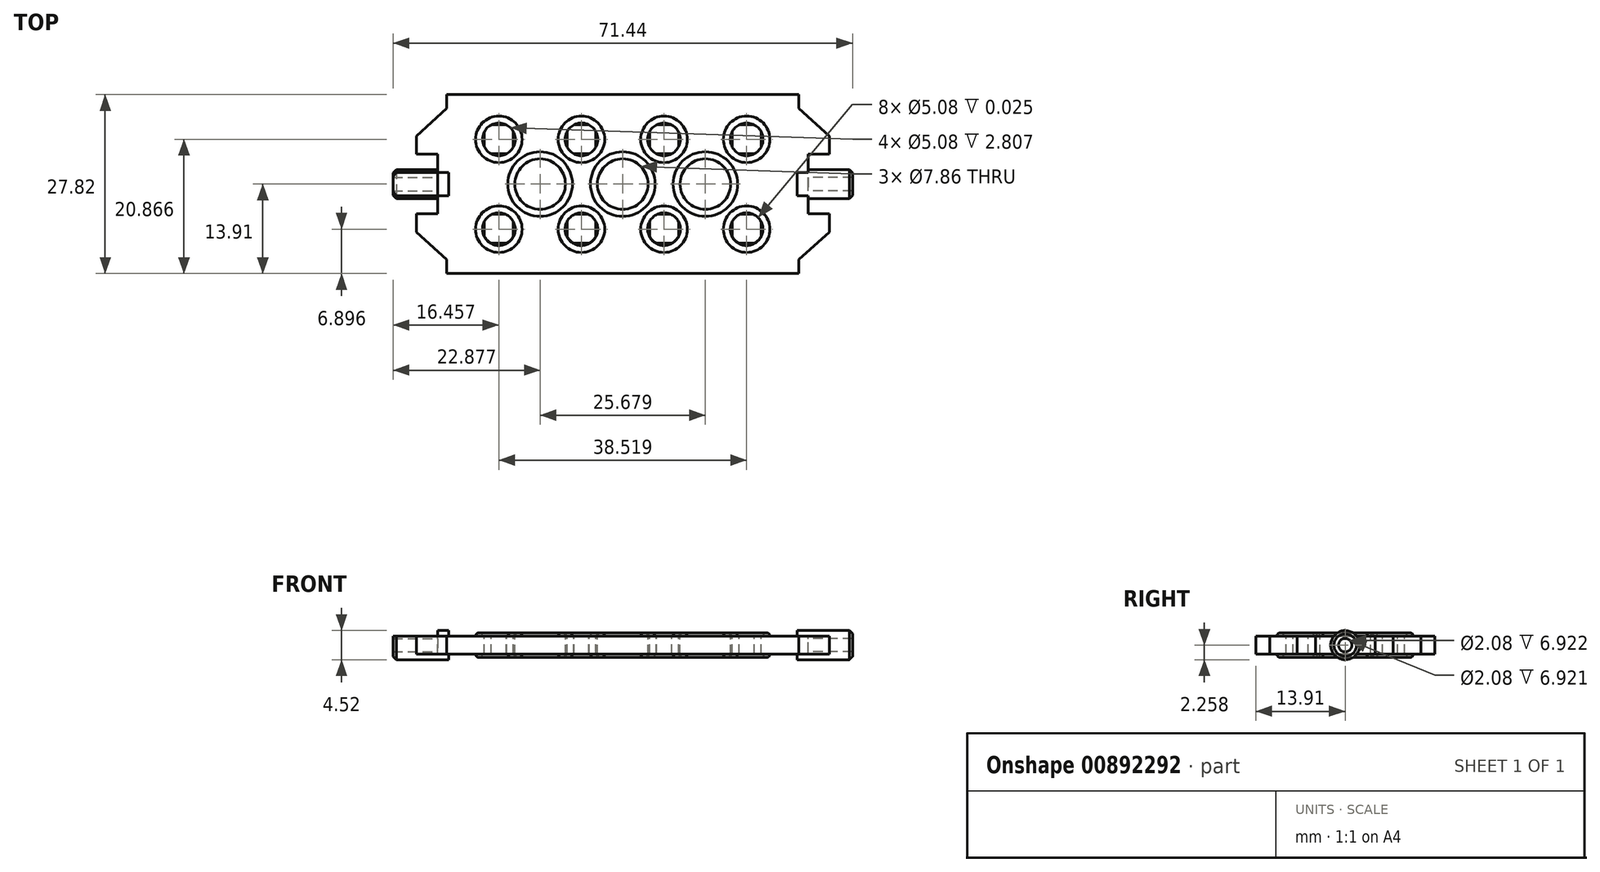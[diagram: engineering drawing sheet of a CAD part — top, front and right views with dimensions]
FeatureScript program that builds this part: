
annotation { "Feature Type Name" : "Feature", "Feature Type Description" : "" }
export const myFeature = defineFeature(function(context is Context, id is Id, definition is map)
    precondition{}
    {
        {
            var Q0;
            Q0=qCreatedBy(makeId("Top.planeOp"),FACE);
            var sketch = newSketch(context, id + "F0", { "sketchPlane" : qUnion([Q0])});
            skLineSegment(sketch, "E0.bottom", {"start": v(-32.7, 12.97) * mm, "end": v(31.5, 12.97) * mm});
            skLineSegment(sketch, "E0.top", {"start": v(-32.7, -14.85) * mm, "end": v(31.5, -14.85) * mm});
            skLineSegment(sketch, "E0.left", {"start": v(-32.7, 12.97) * mm, "end": v(-32.7, -14.85) * mm});
            skLineSegment(sketch, "E0.right", {"start": v(31.5, 12.97) * mm, "end": v(31.5, -14.85) * mm});
            skSolve(sketch);
        }
        {
            var Q0;
            Q0 = qSketchRegion(id + "F0", true);
            extrude(context, id + "F1", {"entities" : qUnion([Q0]), "depth" : 2.76 * mm, "offsetDistance" : 25.4 * mm});
        }
        {
            var Q0;
            Q0=makeQuery(id+"F1.opExtrude","CAP_FACE",FACE,{"disambiguationData":[OSD([sQuery(id+"F0.wireOp",EDGE,"E0.bottom"),sQuery(id+"F0.wireOp",EDGE,"E0.top"),sQuery(id+"F0.wireOp",EDGE,"E0.left"),sQuery(id+"F0.wireOp",EDGE,"E0.right")])],"isStart":false});
            var sketch = newSketch(context, id + "F2", { "sketchPlane" : qUnion([Q0])});
            skLineSegment(sketch, "E1", {"start": v(-32.7, -0.94) * mm, "end": v(31.5, -0.94) * mm, "construction": true});
            skPoint(sketch, "E2", {"position": v(26.78, 12.97) * mm});
            skLineSegment(sketch, "E3", {"start": v(28.2, 3.7) * mm, "end": v(28.2, -5.58) * mm});
            skLineSegment(sketch, "E4", {"start": v(26.78, 12.97) * mm, "end": v(26.78, 10.8) * mm});
            skLineSegment(sketch, "E5", {"start": v(28.2, 3.7) * mm, "end": v(31.5, 3.7) * mm});
            skLineSegment(sketch, "E6", {"start": v(28.2, -5.58) * mm, "end": v(31.5, -5.58) * mm});
            skLineSegment(sketch, "E7", {"start": v(28.2, -0.94) * mm, "end": v(28.2, -5.58) * mm});
            skLineSegment(sketch, "E8", {"start": v(31.5, -0.94) * mm, "end": v(31.5, 3.7) * mm});
            skLineSegment(sketch, "E9", {"start": v(31.5, 3.7) * mm, "end": v(31.5, 6.51) * mm});
            skLineSegment(sketch, "E10", {"start": v(31.5, -5.58) * mm, "end": v(31.5, -8.4) * mm});
            skPoint(sketch, "E11", {"position": v(26.78, -14.85) * mm});
            skLineSegment(sketch, "E12", {"start": v(26.78, -14.85) * mm, "end": v(26.78, -12.68) * mm});
            skLineSegment(sketch, "E13", {"start": v(26.78, -12.68) * mm, "end": v(31.5, -8.4) * mm});
            skLineSegment(sketch, "E14", {"start": v(26.78, 10.8) * mm, "end": v(31.5, 6.51) * mm});
            skPoint(sketch, "E15", {"position": v(-27.97, -14.85) * mm});
            skPoint(sketch, "E16", {"position": v(-27.97, 12.97) * mm});
            skLineSegment(sketch, "E17", {"start": v(-29.4, -0.94) * mm, "end": v(-29.4, 3.7) * mm});
            skLineSegment(sketch, "E18", {"start": v(-29.4, -0.94) * mm, "end": v(-29.4, -5.58) * mm});
            skLineSegment(sketch, "E19", {"start": v(-29.4, -5.58) * mm, "end": v(-32.7, -5.58) * mm});
            skLineSegment(sketch, "E20", {"start": v(-29.4, 3.7) * mm, "end": v(-32.7, 3.7) * mm});
            skLineSegment(sketch, "E21", {"start": v(-27.97, 12.97) * mm, "end": v(-27.97, 10.8) * mm});
            skLineSegment(sketch, "E22", {"start": v(-27.97, -14.85) * mm, "end": v(-27.97, -12.68) * mm});
            skLineSegment(sketch, "E23", {"start": v(-32.7, -5.58) * mm, "end": v(-32.7, -8.4) * mm});
            skLineSegment(sketch, "E24", {"start": v(-32.7, 3.7) * mm, "end": v(-32.7, 6.51) * mm});
            skLineSegment(sketch, "E25", {"start": v(-32.7, 6.51) * mm, "end": v(-27.97, 10.8) * mm});
            skLineSegment(sketch, "E26", {"start": v(-27.97, -12.68) * mm, "end": v(-32.7, -8.4) * mm});
            skCircle(sketch, "E27", {"center": v(-0.6, -0.94) * mm, "radius": 3.93 * mm});
            skLineSegment(sketch, "E28", {"start": v(31.5, 6.02) * mm, "end": v(-32.7, 6.02) * mm, "construction": true});
            skLineSegment(sketch, "E29", {"start": v(31.5, -0.94) * mm, "end": v(31.5, 12.97) * mm, "construction": true});
            skPoint(sketch, "E30", {"position": v(-7.01, 6.02) * mm});
            skPoint(sketch, "E31", {"position": v(5.83, 6.02) * mm});
            skPoint(sketch, "E32", {"position": v(18.67, 6.02) * mm});
            skPoint(sketch, "E33", {"position": v(31.5, 6.02) * mm});
            skPoint(sketch, "E34", {"position": v(-19.85, 6.02) * mm});
            skLineSegment(sketch, "E35", {"start": v(-19.85, -14.85) * mm, "end": v(-19.85, 6.02) * mm, "construction": true});
            skLineSegment(sketch, "E36", {"start": v(-7.01, 6.02) * mm, "end": v(-7.01, -14.85) * mm, "construction": true});
            skLineSegment(sketch, "E37", {"start": v(5.83, 6.02) * mm, "end": v(5.83, -14.85) * mm, "construction": true});
            skLineSegment(sketch, "E38", {"start": v(18.67, 6.02) * mm, "end": v(18.67, -14.85) * mm, "construction": true});
            skLineSegment(sketch, "E39", {"start": v(31.5, -0.94) * mm, "end": v(31.5, -14.85) * mm, "construction": true});
            skPoint(sketch, "E40", {"position": v(31.5, -7.9) * mm});
            skLineSegment(sketch, "E41", {"start": v(31.5, -7.9) * mm, "end": v(-32.7, -7.9) * mm, "construction": true});
            skCircle(sketch, "E42", {"center": v(-19.85, -7.9) * mm, "radius": 2.54 * mm});
            skCircle(sketch, "E43", {"center": v(-19.85, 6.02) * mm, "radius": 2.54 * mm});
            skCircle(sketch, "E44", {"center": v(-7.01, 6.02) * mm, "radius": 2.54 * mm});
            skCircle(sketch, "E45", {"center": v(5.83, 6.02) * mm, "radius": 2.54 * mm});
            skCircle(sketch, "E46", {"center": v(18.67, 6.02) * mm, "radius": 2.54 * mm});
            skCircle(sketch, "E47", {"center": v(-7.01, -7.9) * mm, "radius": 2.54 * mm});
            skCircle(sketch, "E48", {"center": v(18.67, -7.9) * mm, "radius": 2.54 * mm});
            skCircle(sketch, "E49", {"center": v(5.83, -7.9) * mm, "radius": 2.54 * mm});
            skPoint(sketch, "E50", {"position": v(5.83, -0.94) * mm});
            skPoint(sketch, "E51", {"position": v(18.67, -0.94) * mm});
            skPoint(sketch, "E52", {"position": v(-7.01, -0.94) * mm});
            skPoint(sketch, "E53", {"position": v(-19.85, -0.94) * mm});
            skLineSegment(sketch, "E54", {"start": v(18.67, -0.94) * mm, "end": v(5.83, -0.94) * mm});
            skLineSegment(sketch, "E55", {"start": v(-19.85, -0.94) * mm, "end": v(-7.01, -0.94) * mm});
            skCircle(sketch, "E56", {"center": v(12.25, -0.94) * mm, "radius": 3.93 * mm});
            skCircle(sketch, "E57", {"center": v(-13.43, -0.94) * mm, "radius": 3.93 * mm});
            skLineSegment(sketch, "E58.bottom", {"start": v(16.42, -10.14) * mm, "end": v(20.91, -10.14) * mm});
            skLineSegment(sketch, "E58.top", {"start": v(16.42, -5.65) * mm, "end": v(20.91, -5.65) * mm});
            skLineSegment(sketch, "E58.left", {"start": v(16.42, -10.14) * mm, "end": v(16.42, -5.65) * mm});
            skLineSegment(sketch, "E58.right", {"start": v(20.91, -10.14) * mm, "end": v(20.91, -5.65) * mm});
            skLineSegment(sketch, "E59.0.1.0", {"start": v(16.42, 3.77) * mm, "end": v(20.91, 3.77) * mm});
            skLineSegment(sketch, "E59.0.1.1", {"start": v(16.42, 3.77) * mm, "end": v(16.42, 8.27) * mm});
            skLineSegment(sketch, "E59.0.1.2", {"start": v(16.42, 8.27) * mm, "end": v(20.91, 8.27) * mm});
            skLineSegment(sketch, "E59.0.1.3", {"start": v(20.91, 3.77) * mm, "end": v(20.91, 8.27) * mm});
            skLineSegment(sketch, "E59.1.0.0", {"start": v(3.58, -10.14) * mm, "end": v(8.07, -10.14) * mm});
            skLineSegment(sketch, "E59.1.0.1", {"start": v(3.58, -10.14) * mm, "end": v(3.58, -5.65) * mm});
            skLineSegment(sketch, "E59.1.0.2", {"start": v(3.58, -5.65) * mm, "end": v(8.07, -5.65) * mm});
            skLineSegment(sketch, "E59.1.0.3", {"start": v(8.07, -10.14) * mm, "end": v(8.07, -5.65) * mm});
            skLineSegment(sketch, "E59.1.1.0", {"start": v(3.58, 3.77) * mm, "end": v(8.07, 3.77) * mm});
            skLineSegment(sketch, "E59.1.1.1", {"start": v(3.58, 3.77) * mm, "end": v(3.58, 8.27) * mm});
            skLineSegment(sketch, "E59.1.1.2", {"start": v(3.58, 8.27) * mm, "end": v(8.07, 8.27) * mm});
            skLineSegment(sketch, "E59.1.1.3", {"start": v(8.07, 3.77) * mm, "end": v(8.07, 8.27) * mm});
            skLineSegment(sketch, "E59.2.0.0", {"start": v(-9.26, -10.14) * mm, "end": v(-4.76, -10.14) * mm});
            skLineSegment(sketch, "E59.2.0.1", {"start": v(-9.26, -10.14) * mm, "end": v(-9.26, -5.65) * mm});
            skLineSegment(sketch, "E59.2.0.2", {"start": v(-9.26, -5.65) * mm, "end": v(-4.76, -5.65) * mm});
            skLineSegment(sketch, "E59.2.0.3", {"start": v(-4.76, -10.14) * mm, "end": v(-4.76, -5.65) * mm});
            skLineSegment(sketch, "E59.2.1.0", {"start": v(-9.26, 3.77) * mm, "end": v(-4.76, 3.77) * mm});
            skLineSegment(sketch, "E59.2.1.1", {"start": v(-9.26, 3.77) * mm, "end": v(-9.26, 8.27) * mm});
            skLineSegment(sketch, "E59.2.1.2", {"start": v(-9.26, 8.27) * mm, "end": v(-4.76, 8.27) * mm});
            skLineSegment(sketch, "E59.2.1.3", {"start": v(-4.76, 3.77) * mm, "end": v(-4.76, 8.27) * mm});
            skLineSegment(sketch, "E59.3.0.0", {"start": v(-22.1, -10.14) * mm, "end": v(-17.6, -10.14) * mm});
            skLineSegment(sketch, "E59.3.0.1", {"start": v(-22.1, -10.14) * mm, "end": v(-22.1, -5.65) * mm});
            skLineSegment(sketch, "E59.3.0.2", {"start": v(-22.1, -5.65) * mm, "end": v(-17.6, -5.65) * mm});
            skLineSegment(sketch, "E59.3.0.3", {"start": v(-17.6, -10.14) * mm, "end": v(-17.6, -5.65) * mm});
            skLineSegment(sketch, "E59.3.1.0", {"start": v(-22.1, 3.77) * mm, "end": v(-17.6, 3.77) * mm});
            skLineSegment(sketch, "E59.3.1.1", {"start": v(-22.1, 3.77) * mm, "end": v(-22.1, 8.27) * mm});
            skLineSegment(sketch, "E59.3.1.2", {"start": v(-22.1, 8.27) * mm, "end": v(-17.6, 8.27) * mm});
            skLineSegment(sketch, "E59.3.1.3", {"start": v(-17.6, 3.77) * mm, "end": v(-17.6, 8.27) * mm});
            skLineSegment(sketch, "E59.direction1", {"start": v(16.42, -10.14) * mm, "end": v(3.58, -10.14) * mm, "construction": true});
            skLineSegment(sketch, "E59.direction2", {"start": v(16.42, -10.14) * mm, "end": v(16.42, 3.77) * mm, "construction": true});
            skSolve(sketch);
        }
        {
            var Q0;
            Q0=makeQuery(id+"F2.imprint","IMPRINT",FACE,{"disambiguationData":[TD([[makeQuery(id+"F2.imprint","IMPRINT",EDGE,{"derivedFrom":sQuery(id+"F2.wireOp",EDGE,"E3")}),1.0]])]});
            var Q1;
            {var subQ0=sQuery(id+"F2.wireOp",EDGE,"E4");Q1=makeQuery(id+"F2.imprint","IMPRINT",FACE,{"disambiguationData":[TD([[makeQuery(id+"F2.imprint","IMPRINT",EDGE,{"derivedFrom":subQ0}),1.0]])]});}
            var Q2;
            {var subQ0=sQuery(id+"F2.wireOp",EDGE,"E12");Q2=makeQuery(id+"F2.imprint","IMPRINT",FACE,{"disambiguationData":[TD([[makeQuery(id+"F2.imprint","IMPRINT",EDGE,{"derivedFrom":subQ0}),-1.0]])]});}
            var Q3;
            {var subQ0=sQuery(id+"F2.wireOp",EDGE,"E22");Q3=makeQuery(id+"F2.imprint","IMPRINT",FACE,{"disambiguationData":[TD([[makeQuery(id+"F2.imprint","IMPRINT",EDGE,{"derivedFrom":subQ0}),1.0]])]});}
            var Q4;
            Q4=makeQuery(id+"F2.imprint","IMPRINT",FACE,{"disambiguationData":[TD([[makeQuery(id+"F2.imprint","IMPRINT",EDGE,{"derivedFrom":sQuery(id+"F2.wireOp",EDGE,"E17")}),1.0]])]});
            var Q5;
            {var subQ0=sQuery(id+"F2.wireOp",EDGE,"E21");Q5=makeQuery(id+"F2.imprint","IMPRINT",FACE,{"disambiguationData":[TD([[makeQuery(id+"F2.imprint","IMPRINT",EDGE,{"derivedFrom":subQ0}),-1.0]])]});}
            extrude(context, id + "F3", {"entities" : qUnion([Q0, Q1, Q2, Q3, Q4, Q5]), "operationType" : NewBodyOperationType.REMOVE, "oppositeDirection" : true, "depth" : 25.4 * mm, "offsetDistance" : 25.4 * mm});
        }
        {
            var Q0;
            Q0=makeQuery(id+"F2.imprint","IMPRINT",FACE,{"disambiguationData":[TD([[makeQuery(id+"F2.imprint","IMPRINT",EDGE,{"derivedFrom":sQuery(id+"F2.wireOp",EDGE,"E43")}),1.0]])]});
            var Q1;
            {var subQ0=sQuery(id+"F2.wireOp",EDGE,"E57");var subQ1=sQuery(id+"F2.wireOp",EDGE,"E55");var subQ2=makeQuery(id+"F2.imprint","INTERSECT",VERTEX,{"disambiguationData":[OD(0.0)],"derivedFrom":[subQ1,subQ0]});Q1=makeQuery(id+"F2.imprint","IMPRINT",FACE,{"disambiguationData":[TD([[makeQuery(id+"F2.imprint","IMPRINT",EDGE,{"disambiguationData":[TD([[subQ2,-1.0]])],"derivedFrom":subQ1}),-1.0]])]});}
            var Q2;
            {var subQ0=sQuery(id+"F2.wireOp",EDGE,"E57");var subQ1=sQuery(id+"F2.wireOp",EDGE,"E55");var subQ2=makeQuery(id+"F2.imprint","INTERSECT",VERTEX,{"disambiguationData":[OD(0.0)],"derivedFrom":[subQ1,subQ0]});Q2=makeQuery(id+"F2.imprint","IMPRINT",FACE,{"disambiguationData":[TD([[makeQuery(id+"F2.imprint","IMPRINT",EDGE,{"disambiguationData":[TD([[subQ2,-1.0]])],"derivedFrom":subQ1}),1.0]])]});}
            var Q3;
            Q3=makeQuery(id+"F2.imprint","IMPRINT",FACE,{"disambiguationData":[TD([[makeQuery(id+"F2.imprint","IMPRINT",EDGE,{"derivedFrom":sQuery(id+"F2.wireOp",EDGE,"E27")}),1.0]])]});
            var Q4;
            {var subQ0=sQuery(id+"F2.wireOp",EDGE,"E56");var subQ1=sQuery(id+"F2.wireOp",EDGE,"E54");var subQ2=makeQuery(id+"F2.imprint","INTERSECT",VERTEX,{"disambiguationData":[OD(0.0)],"derivedFrom":[subQ1,subQ0]});Q4=makeQuery(id+"F2.imprint","IMPRINT",FACE,{"disambiguationData":[TD([[makeQuery(id+"F2.imprint","IMPRINT",EDGE,{"disambiguationData":[TD([[subQ2,1.0]])],"derivedFrom":subQ1}),1.0]])]});}
            var Q5;
            {var subQ0=sQuery(id+"F2.wireOp",EDGE,"E56");var subQ1=sQuery(id+"F2.wireOp",EDGE,"E54");var subQ2=makeQuery(id+"F2.imprint","INTERSECT",VERTEX,{"disambiguationData":[OD(0.0)],"derivedFrom":[subQ1,subQ0]});Q5=makeQuery(id+"F2.imprint","IMPRINT",FACE,{"disambiguationData":[TD([[makeQuery(id+"F2.imprint","IMPRINT",EDGE,{"disambiguationData":[TD([[subQ2,1.0]])],"derivedFrom":subQ1}),-1.0]])]});}
            var Q6;
            Q6=makeQuery(id+"F2.imprint","IMPRINT",FACE,{"disambiguationData":[TD([[makeQuery(id+"F2.imprint","IMPRINT",EDGE,{"derivedFrom":sQuery(id+"F2.wireOp",EDGE,"E45")}),1.0]])]});
            var Q7;
            Q7=makeQuery(id+"F2.imprint","IMPRINT",FACE,{"disambiguationData":[TD([[makeQuery(id+"F2.imprint","IMPRINT",EDGE,{"derivedFrom":sQuery(id+"F2.wireOp",EDGE,"E44")}),1.0]])]});
            var Q8;
            Q8=makeQuery(id+"F2.imprint","IMPRINT",FACE,{"disambiguationData":[TD([[makeQuery(id+"F2.imprint","IMPRINT",EDGE,{"derivedFrom":sQuery(id+"F2.wireOp",EDGE,"E47")}),1.0]])]});
            var Q9;
            Q9=makeQuery(id+"F2.imprint","IMPRINT",FACE,{"disambiguationData":[TD([[makeQuery(id+"F2.imprint","IMPRINT",EDGE,{"derivedFrom":sQuery(id+"F2.wireOp",EDGE,"E42")}),1.0]])]});
            var Q10;
            Q10=makeQuery(id+"F2.imprint","IMPRINT",FACE,{"disambiguationData":[TD([[makeQuery(id+"F2.imprint","IMPRINT",EDGE,{"derivedFrom":sQuery(id+"F2.wireOp",EDGE,"E49")}),1.0]])]});
            var Q11;
            Q11=makeQuery(id+"F2.imprint","IMPRINT",FACE,{"disambiguationData":[TD([[makeQuery(id+"F2.imprint","IMPRINT",EDGE,{"derivedFrom":sQuery(id+"F2.wireOp",EDGE,"E48")}),1.0]])]});
            var Q12;
            Q12=makeQuery(id+"F2.imprint","IMPRINT",FACE,{"disambiguationData":[TD([[makeQuery(id+"F2.imprint","IMPRINT",EDGE,{"derivedFrom":sQuery(id+"F2.wireOp",EDGE,"E46")}),1.0]])]});
            extrude(context, id + "F4", {"entities" : qUnion([Q0, Q1, Q2, Q3, Q4, Q5, Q6, Q7, Q8, Q9, Q10, Q11, Q12]), "operationType" : NewBodyOperationType.REMOVE, "oppositeDirection" : true, "depth" : 25.4 * mm, "offsetDistance" : 25.4 * mm});
        }
        {
            var Q0;
            Q0=makeQuery(id+"F3.boolean.opBoolean","COPY",FACE,{"derivedFrom":makeQuery(id+"F3.opExtrude","SWEPT_FACE",FACE,{"disambiguationData":[OSD([sQuery(id+"F2.wireOp",EDGE,"E17"),sQuery(id+"F2.wireOp",EDGE,"E18")])]})});
            var sketch = newSketch(context, id + "F5", { "sketchPlane" : qUnion([Q0])});
            skLineSegment(sketch, "E60", {"start": v(0.94, 0) * mm, "end": v(0.94, 2.76) * mm, "construction": true});
            skCircle(sketch, "E61", {"center": v(0.94, 1.38) * mm, "radius": 2.26 * mm});
            skCircle(sketch, "E62", {"center": v(0.94, 1.38) * mm, "radius": 1.04 * mm});
            skSolve(sketch);
        }
        {
            var Q0;
            Q0=makeQuery(id+"F5.imprint","IMPRINT",FACE,{"disambiguationData":[TD([[makeQuery(id+"F5.imprint","IMPRINT",EDGE,{"derivedFrom":sQuery(id+"F5.wireOp",EDGE,"E62")}),-1.0]])]});
            var Q1;
            {var subQ0=sQuery(id+"F5.wireOp",EDGE,"E61");var subQ1=makeQuery(id+"F3.boolean.opBoolean","COPY",EDGE,{"derivedFrom":makeQuery(id+"F3.opExtrude","CAP_EDGE",EDGE,{"disambiguationData":[OSD([sQuery(id+"F2.wireOp",EDGE,"E17"),sQuery(id+"F2.wireOp",EDGE,"E18")])],"isStart":true})});var subQ2=makeQuery(id+"F5.imprint","INTERSECT",VERTEX,{"disambiguationData":[OD(0.0)],"derivedFrom":[subQ1,subQ0]});Q1=makeQuery(id+"F5.imprint","IMPRINT",FACE,{"disambiguationData":[TD([[makeQuery(id+"F5.imprint","IMPRINT",EDGE,{"disambiguationData":[TD([[subQ2,1.0]])],"derivedFrom":subQ0}),1.0]])]});}
            var Q2;
            {var subQ0=sQuery(id+"F5.wireOp",EDGE,"E61");var subQ1=makeQuery(id+"F3.boolean.opBoolean","INTERSECT",EDGE,{"derivedFrom":[makeQuery(id+"F1.opExtrude","CAP_FACE",FACE,{"disambiguationData":[OSD([sQuery(id+"F0.wireOp",EDGE,"E0.bottom"),sQuery(id+"F0.wireOp",EDGE,"E0.top"),sQuery(id+"F0.wireOp",EDGE,"E0.left"),sQuery(id+"F0.wireOp",EDGE,"E0.right")])],"isStart":true}),makeQuery(id+"F3.opExtrude","SWEPT_FACE",FACE,{"disambiguationData":[OSD([sQuery(id+"F2.wireOp",EDGE,"E17"),sQuery(id+"F2.wireOp",EDGE,"E18")])]})]});var subQ2=makeQuery(id+"F5.imprint","INTERSECT",VERTEX,{"disambiguationData":[OD(0.0)],"derivedFrom":[subQ1,subQ0]});Q2=makeQuery(id+"F5.imprint","IMPRINT",FACE,{"disambiguationData":[TD([[makeQuery(id+"F5.imprint","IMPRINT",EDGE,{"disambiguationData":[TD([[subQ2,-1.0]])],"derivedFrom":subQ0}),1.0]])]});}
            extrude(context, id + "F6", {"entities" : qUnion([Q0, Q1, Q2]), "operationType" : NewBodyOperationType.ADD, "depth" : 6.92 * mm, "offsetDistance" : 25.4 * mm});
        }
        {
            var Q0;
            Q0=makeQuery(id+"F3.boolean.opBoolean","COPY",FACE,{"derivedFrom":makeQuery(id+"F3.opExtrude","SWEPT_FACE",FACE,{"disambiguationData":[OSD([sQuery(id+"F2.wireOp",EDGE,"E3"),sQuery(id+"F2.wireOp",EDGE,"E7")])]})});
            var sketch = newSketch(context, id + "F7", { "sketchPlane" : qUnion([Q0])});
            skCircle(sketch, "E63.0", {"center": v(-0.94, 1.38) * mm, "radius": 2.26 * mm});
            skCircle(sketch, "E63.1", {"center": v(-0.94, 1.38) * mm, "radius": 1.04 * mm});
            skSolve(sketch);
        }
        {
            var Q0;
            Q0 = qSketchRegion(id + "F7", true);
            extrude(context, id + "F8", {"entities" : qUnion([Q0]), "operationType" : NewBodyOperationType.ADD, "depth" : 6.92 * mm, "offsetDistance" : 25.4 * mm});
        }
        {
            var Q0;
            {var subQ0=sQuery(id+"F5.wireOp",EDGE,"E61");Q0=makeQuery(id+"F6.boolean.opBoolean","SPLIT",FACE,{"disambiguationData":[TD([makeQuery(id+"F1.opExtrude","CAP_FACE",FACE,{"disambiguationData":[OSD([sQuery(id+"F0.wireOp",EDGE,"E0.bottom"),sQuery(id+"F0.wireOp",EDGE,"E0.top"),sQuery(id+"F0.wireOp",EDGE,"E0.left"),sQuery(id+"F0.wireOp",EDGE,"E0.right")])],"isStart":false})])],"derivedFrom":makeQuery(id+"F6.opExtrude","CAP_FACE",FACE,{"disambiguationData":[OSD([subQ0,sQuery(id+"F5.wireOp",EDGE,"E62")])],"isStart":true})});}
            var sketch = newSketch(context, id + "F9", { "sketchPlane" : qUnion([Q0])});
            skCircle(sketch, "E64.0.0", {"center": v(-0.94, 1.38) * mm, "radius": 2.26 * mm});
            skSolve(sketch);
        }
        {
            var Q0;
            Q0 = qSketchRegion(id + "F9", true);
            extrude(context, id + "F10", {"entities" : qUnion([Q0]), "operationType" : NewBodyOperationType.ADD, "depth" : 1.71 * mm, "offsetDistance" : 25.4 * mm});
        }
        {
            var Q0;
            {var subQ0=sQuery(id+"F7.wireOp",EDGE,"E63.0");Q0=makeQuery(id+"F8.boolean.opBoolean","SPLIT",FACE,{"disambiguationData":[TD([makeQuery(id+"F1.opExtrude","CAP_FACE",FACE,{"disambiguationData":[OSD([sQuery(id+"F0.wireOp",EDGE,"E0.bottom"),sQuery(id+"F0.wireOp",EDGE,"E0.top"),sQuery(id+"F0.wireOp",EDGE,"E0.left"),sQuery(id+"F0.wireOp",EDGE,"E0.right")])],"isStart":false})])],"derivedFrom":makeQuery(id+"F8.opExtrude","CAP_FACE",FACE,{"disambiguationData":[OSD([subQ0,sQuery(id+"F7.wireOp",EDGE,"E63.1")])],"isStart":true})});}
            var sketch = newSketch(context, id + "F11", { "sketchPlane" : qUnion([Q0])});
            skCircle(sketch, "E65.0", {"center": v(0.94, 1.38) * mm, "radius": 2.26 * mm});
            skCircle(sketch, "E65.1", {"center": v(0.94, 1.38) * mm, "radius": 1.04 * mm});
            skSolve(sketch);
        }
        {
            var Q0;
            Q0 = qSketchRegion(id + "F11", true);
            extrude(context, id + "F12", {"entities" : qUnion([Q0]), "operationType" : NewBodyOperationType.ADD, "depth" : 1.71 * mm, "offsetDistance" : 25.4 * mm});
        }
        {
            var Q0;
            Q0=makeQuery(id+"F1.opExtrude","CAP_FACE",FACE,{"disambiguationData":[OSD([sQuery(id+"F0.wireOp",EDGE,"E0.bottom"),sQuery(id+"F0.wireOp",EDGE,"E0.top"),sQuery(id+"F0.wireOp",EDGE,"E0.left"),sQuery(id+"F0.wireOp",EDGE,"E0.right")])],"isStart":false});
            var sketch = newSketch(context, id + "F13", { "sketchPlane" : qUnion([Q0])});
            skCircle(sketch, "E66", {"center": v(-19.85, 6.02) * mm, "radius": 3.62 * mm});
            skCircle(sketch, "E67.0", {"center": v(-19.85, 6.02) * mm, "radius": 2.54 * mm});
            skCircle(sketch, "E68.0.1.0", {"center": v(-19.85, -7.95) * mm, "radius": 2.54 * mm});
            skCircle(sketch, "E68.0.1.1", {"center": v(-19.85, -7.95) * mm, "radius": 3.62 * mm});
            skCircle(sketch, "E68.1.0.0", {"center": v(-7.01, 6.02) * mm, "radius": 2.54 * mm});
            skCircle(sketch, "E68.1.0.1", {"center": v(-7.01, 6.02) * mm, "radius": 3.62 * mm});
            skCircle(sketch, "E68.1.1.0", {"center": v(-7.01, -7.95) * mm, "radius": 2.54 * mm});
            skCircle(sketch, "E68.1.1.1", {"center": v(-7.01, -7.95) * mm, "radius": 3.62 * mm});
            skCircle(sketch, "E68.2.0.0", {"center": v(5.83, 6.02) * mm, "radius": 2.54 * mm});
            skCircle(sketch, "E68.2.0.1", {"center": v(5.83, 6.02) * mm, "radius": 3.62 * mm});
            skCircle(sketch, "E68.2.1.0", {"center": v(5.83, -7.95) * mm, "radius": 2.54 * mm});
            skCircle(sketch, "E68.2.1.1", {"center": v(5.83, -7.95) * mm, "radius": 3.62 * mm});
            skCircle(sketch, "E68.3.0.0", {"center": v(18.67, 6.02) * mm, "radius": 2.54 * mm});
            skCircle(sketch, "E68.3.0.1", {"center": v(18.67, 6.02) * mm, "radius": 3.62 * mm});
            skCircle(sketch, "E68.3.1.0", {"center": v(18.67, -7.95) * mm, "radius": 2.54 * mm});
            skCircle(sketch, "E68.3.1.1", {"center": v(18.67, -7.95) * mm, "radius": 3.62 * mm});
            skLineSegment(sketch, "E68.direction1", {"start": v(-19.85, 6.02) * mm, "end": v(-7.01, 6.02) * mm, "construction": true});
            skLineSegment(sketch, "E68.direction2", {"start": v(-19.85, 6.02) * mm, "end": v(-19.85, -7.95) * mm, "construction": true});
            skCircle(sketch, "E69", {"center": v(12.25, -0.94) * mm, "radius": 5.02 * mm});
            skCircle(sketch, "E70", {"center": v(-0.6, -0.94) * mm, "radius": 5.02 * mm});
            skCircle(sketch, "E71", {"center": v(-13.43, -0.94) * mm, "radius": 5.02 * mm});
            skCircle(sketch, "E72.0", {"center": v(12.25, -0.94) * mm, "radius": 3.93 * mm});
            skCircle(sketch, "E72.1", {"center": v(-0.6, -0.94) * mm, "radius": 3.93 * mm});
            skCircle(sketch, "E72.2", {"center": v(-13.43, -0.94) * mm, "radius": 3.93 * mm});
            skSolve(sketch);
        }
        {
            var Q0;
            Q0 = qSketchRegion(id + "F13", true);
            extrude(context, id + "F14", {"entities" : qUnion([Q0]), "operationType" : NewBodyOperationType.ADD, "depth" : 0.53 * mm, "offsetDistance" : 25.4 * mm});
        }
        {
            var Q0;
            Q0=makeQuery(id+"F1.opExtrude","CAP_FACE",FACE,{"disambiguationData":[OSD([sQuery(id+"F0.wireOp",EDGE,"E0.bottom"),sQuery(id+"F0.wireOp",EDGE,"E0.top"),sQuery(id+"F0.wireOp",EDGE,"E0.left"),sQuery(id+"F0.wireOp",EDGE,"E0.right")])],"isStart":true});
            var sketch = newSketch(context, id + "F15", { "sketchPlane" : qUnion([Q0])});
            skCircle(sketch, "E73.0", {"center": v(-19.85, -6.02) * mm, "radius": 2.54 * mm});
            skCircle(sketch, "E73.1", {"center": v(-19.85, -6.02) * mm, "radius": 3.62 * mm});
            skCircle(sketch, "E74.0.1.0", {"center": v(-19.85, 7.95) * mm, "radius": 3.62 * mm});
            skCircle(sketch, "E74.0.1.1", {"center": v(-19.85, 7.95) * mm, "radius": 2.54 * mm});
            skCircle(sketch, "E74.1.0.0", {"center": v(-7.01, -6.02) * mm, "radius": 3.62 * mm});
            skCircle(sketch, "E74.1.0.1", {"center": v(-7.01, -6.02) * mm, "radius": 2.54 * mm});
            skCircle(sketch, "E74.1.1.0", {"center": v(-7.01, 7.95) * mm, "radius": 3.62 * mm});
            skCircle(sketch, "E74.1.1.1", {"center": v(-7.01, 7.95) * mm, "radius": 2.54 * mm});
            skCircle(sketch, "E74.2.0.0", {"center": v(5.83, -6.02) * mm, "radius": 3.62 * mm});
            skCircle(sketch, "E74.2.0.1", {"center": v(5.83, -6.02) * mm, "radius": 2.54 * mm});
            skCircle(sketch, "E74.2.1.0", {"center": v(5.83, 7.95) * mm, "radius": 3.62 * mm});
            skCircle(sketch, "E74.2.1.1", {"center": v(5.83, 7.95) * mm, "radius": 2.54 * mm});
            skCircle(sketch, "E74.3.0.0", {"center": v(18.67, -6.02) * mm, "radius": 3.62 * mm});
            skCircle(sketch, "E74.3.0.1", {"center": v(18.67, -6.02) * mm, "radius": 2.54 * mm});
            skCircle(sketch, "E74.3.1.0", {"center": v(18.67, 7.95) * mm, "radius": 3.62 * mm});
            skCircle(sketch, "E74.3.1.1", {"center": v(18.67, 7.95) * mm, "radius": 2.54 * mm});
            skLineSegment(sketch, "E74.direction1", {"start": v(-19.85, -6.02) * mm, "end": v(-7.01, -6.02) * mm, "construction": true});
            skLineSegment(sketch, "E74.direction2", {"start": v(-19.85, -6.02) * mm, "end": v(-19.85, 7.95) * mm, "construction": true});
            skCircle(sketch, "E75.0", {"center": v(12.25, 0.94) * mm, "radius": 3.93 * mm});
            skCircle(sketch, "E75.1", {"center": v(12.25, 0.94) * mm, "radius": 5.02 * mm});
            skCircle(sketch, "E75.2", {"center": v(-0.6, 0.94) * mm, "radius": 3.93 * mm});
            skCircle(sketch, "E75.3", {"center": v(-0.6, 0.94) * mm, "radius": 5.02 * mm});
            skCircle(sketch, "E75.4", {"center": v(-13.43, 0.94) * mm, "radius": 3.93 * mm});
            skCircle(sketch, "E75.5", {"center": v(-13.43, 0.94) * mm, "radius": 5.02 * mm});
            skSolve(sketch);
        }
        {
            var Q0;
            Q0 = qSketchRegion(id + "F15", true);
            extrude(context, id + "F16", {"entities" : qUnion([Q0]), "operationType" : NewBodyOperationType.ADD, "depth" : 0.53 * mm, "offsetDistance" : 25.4 * mm});
        }
        {
            var Q0;
            Q0=makeQuery(id+"F6.opExtrude","CAP_EDGE",EDGE,{"disambiguationData":[OSD([sQuery(id+"F5.wireOp",EDGE,"E61")])],"isStart":false});
            var Q1;
            Q1=makeQuery(id+"F8.opExtrude","CAP_EDGE",EDGE,{"disambiguationData":[OSD([sQuery(id+"F7.wireOp",EDGE,"E63.0")])],"isStart":false});
            chamfer(context, id + "F17", {"entities" : qUnion([Q0, Q1]), "width" : 0.5 * mm, "tangentPropagation" : true});
        }
        {
            var Q0;
            Q0=makeQuery(id+"F16.opExtrude","CAP_EDGE",EDGE,{"disambiguationData":[OSD([sQuery(id+"F15.wireOp",EDGE,"E74.3.0.0")])],"isStart":false});
            var Q1;
            Q1=makeQuery(id+"F16.opExtrude","CAP_EDGE",EDGE,{"disambiguationData":[OSD([sQuery(id+"F15.wireOp",EDGE,"E74.3.0.1")])],"isStart":false});
            var Q2;
            Q2=makeQuery(id+"F16.opExtrude","CAP_EDGE",EDGE,{"disambiguationData":[OSD([sQuery(id+"F15.wireOp",EDGE,"E74.2.0.0")])],"isStart":false});
            var Q3;
            Q3=makeQuery(id+"F16.opExtrude","CAP_EDGE",EDGE,{"disambiguationData":[OSD([sQuery(id+"F15.wireOp",EDGE,"E74.2.0.1")])],"isStart":false});
            var Q4;
            Q4=makeQuery(id+"F16.opExtrude","CAP_EDGE",EDGE,{"disambiguationData":[OSD([sQuery(id+"F15.wireOp",EDGE,"E74.1.0.1")])],"isStart":false});
            var Q5;
            Q5=makeQuery(id+"F16.opExtrude","CAP_EDGE",EDGE,{"disambiguationData":[OSD([sQuery(id+"F15.wireOp",EDGE,"E74.1.0.0")])],"isStart":false});
            var Q6;
            Q6=makeQuery(id+"F16.opExtrude","CAP_EDGE",EDGE,{"disambiguationData":[OSD([sQuery(id+"F15.wireOp",EDGE,"E75.2")])],"isStart":false});
            var Q7;
            Q7=makeQuery(id+"F16.opExtrude","CAP_EDGE",EDGE,{"disambiguationData":[OSD([sQuery(id+"F15.wireOp",EDGE,"E75.3")])],"isStart":false});
            var Q8;
            Q8=makeQuery(id+"F16.opExtrude","CAP_EDGE",EDGE,{"disambiguationData":[OSD([sQuery(id+"F15.wireOp",EDGE,"E75.4")])],"isStart":false});
            var Q9;
            Q9=makeQuery(id+"F16.opExtrude","CAP_EDGE",EDGE,{"disambiguationData":[OSD([sQuery(id+"F15.wireOp",EDGE,"E75.5")])],"isStart":false});
            var Q10;
            Q10=makeQuery(id+"F16.opExtrude","CAP_EDGE",EDGE,{"disambiguationData":[OSD([sQuery(id+"F15.wireOp",EDGE,"E75.1")])],"isStart":false});
            var Q11;
            Q11=makeQuery(id+"F16.opExtrude","CAP_EDGE",EDGE,{"disambiguationData":[OSD([sQuery(id+"F15.wireOp",EDGE,"E75.0")])],"isStart":false});
            var Q12;
            Q12=makeQuery(id+"F16.opExtrude","CAP_EDGE",EDGE,{"disambiguationData":[OSD([sQuery(id+"F15.wireOp",EDGE,"E73.1")])],"isStart":false});
            var Q13;
            Q13=makeQuery(id+"F16.opExtrude","CAP_EDGE",EDGE,{"disambiguationData":[OSD([sQuery(id+"F15.wireOp",EDGE,"E73.0")])],"isStart":false});
            var Q14;
            Q14=makeQuery(id+"F16.opExtrude","CAP_EDGE",EDGE,{"disambiguationData":[OSD([sQuery(id+"F15.wireOp",EDGE,"E74.0.1.0")])],"isStart":false});
            var Q15;
            Q15=makeQuery(id+"F16.opExtrude","CAP_EDGE",EDGE,{"disambiguationData":[OSD([sQuery(id+"F15.wireOp",EDGE,"E74.0.1.1")])],"isStart":false});
            var Q16;
            Q16=makeQuery(id+"F16.opExtrude","CAP_EDGE",EDGE,{"disambiguationData":[OSD([sQuery(id+"F15.wireOp",EDGE,"E74.1.1.0")])],"isStart":false});
            var Q17;
            Q17=makeQuery(id+"F16.opExtrude","CAP_EDGE",EDGE,{"disambiguationData":[OSD([sQuery(id+"F15.wireOp",EDGE,"E74.1.1.1")])],"isStart":false});
            var Q18;
            Q18=makeQuery(id+"F16.opExtrude","CAP_EDGE",EDGE,{"disambiguationData":[OSD([sQuery(id+"F15.wireOp",EDGE,"E74.2.1.0")])],"isStart":false});
            var Q19;
            Q19=makeQuery(id+"F16.opExtrude","CAP_EDGE",EDGE,{"disambiguationData":[OSD([sQuery(id+"F15.wireOp",EDGE,"E74.2.1.1")])],"isStart":false});
            var Q20;
            Q20=makeQuery(id+"F16.opExtrude","CAP_EDGE",EDGE,{"disambiguationData":[OSD([sQuery(id+"F15.wireOp",EDGE,"E74.3.1.0")])],"isStart":false});
            var Q21;
            Q21=makeQuery(id+"F16.opExtrude","CAP_EDGE",EDGE,{"disambiguationData":[OSD([sQuery(id+"F15.wireOp",EDGE,"E74.3.1.1")])],"isStart":false});
            var Q22;
            Q22=makeQuery(id+"F14.opExtrude","CAP_EDGE",EDGE,{"disambiguationData":[OSD([sQuery(id+"F13.wireOp",EDGE,"E68.2.0.1")])],"isStart":false});
            var Q23;
            Q23=makeQuery(id+"F14.opExtrude","CAP_EDGE",EDGE,{"disambiguationData":[OSD([sQuery(id+"F13.wireOp",EDGE,"E68.2.0.0")])],"isStart":false});
            var Q24;
            Q24=makeQuery(id+"F14.opExtrude","CAP_EDGE",EDGE,{"disambiguationData":[OSD([sQuery(id+"F13.wireOp",EDGE,"E68.3.0.0")])],"isStart":false});
            var Q25;
            Q25=makeQuery(id+"F14.opExtrude","CAP_EDGE",EDGE,{"disambiguationData":[OSD([sQuery(id+"F13.wireOp",EDGE,"E68.3.0.1")])],"isStart":false});
            var Q26;
            Q26=makeQuery(id+"F14.opExtrude","CAP_EDGE",EDGE,{"disambiguationData":[OSD([sQuery(id+"F13.wireOp",EDGE,"E68.1.0.0")])],"isStart":false});
            var Q27;
            Q27=makeQuery(id+"F14.opExtrude","CAP_EDGE",EDGE,{"disambiguationData":[OSD([sQuery(id+"F13.wireOp",EDGE,"E68.1.0.1")])],"isStart":false});
            var Q28;
            Q28=makeQuery(id+"F14.opExtrude","CAP_EDGE",EDGE,{"disambiguationData":[OSD([sQuery(id+"F13.wireOp",EDGE,"E66")])],"isStart":false});
            var Q29;
            Q29=makeQuery(id+"F14.opExtrude","CAP_EDGE",EDGE,{"disambiguationData":[OSD([sQuery(id+"F13.wireOp",EDGE,"E67.0")])],"isStart":false});
            var Q30;
            Q30=makeQuery(id+"F14.opExtrude","CAP_EDGE",EDGE,{"disambiguationData":[OSD([sQuery(id+"F13.wireOp",EDGE,"E72.2")])],"isStart":false});
            var Q31;
            Q31=makeQuery(id+"F14.opExtrude","CAP_EDGE",EDGE,{"disambiguationData":[OSD([sQuery(id+"F13.wireOp",EDGE,"E71")])],"isStart":false});
            var Q32;
            Q32=makeQuery(id+"F14.opExtrude","CAP_EDGE",EDGE,{"disambiguationData":[OSD([sQuery(id+"F13.wireOp",EDGE,"E72.1")])],"isStart":false});
            var Q33;
            Q33=makeQuery(id+"F14.opExtrude","CAP_EDGE",EDGE,{"disambiguationData":[OSD([sQuery(id+"F13.wireOp",EDGE,"E70")])],"isStart":false});
            var Q34;
            Q34=makeQuery(id+"F14.opExtrude","CAP_EDGE",EDGE,{"disambiguationData":[OSD([sQuery(id+"F13.wireOp",EDGE,"E72.0")])],"isStart":false});
            var Q35;
            Q35=makeQuery(id+"F14.opExtrude","CAP_EDGE",EDGE,{"disambiguationData":[OSD([sQuery(id+"F13.wireOp",EDGE,"E69")])],"isStart":false});
            var Q36;
            Q36=makeQuery(id+"F14.opExtrude","CAP_EDGE",EDGE,{"disambiguationData":[OSD([sQuery(id+"F13.wireOp",EDGE,"E68.2.1.0")])],"isStart":false});
            var Q37;
            Q37=makeQuery(id+"F14.opExtrude","CAP_EDGE",EDGE,{"disambiguationData":[OSD([sQuery(id+"F13.wireOp",EDGE,"E68.2.1.1")])],"isStart":false});
            var Q38;
            Q38=makeQuery(id+"F14.opExtrude","CAP_EDGE",EDGE,{"disambiguationData":[OSD([sQuery(id+"F13.wireOp",EDGE,"E68.1.1.1")])],"isStart":false});
            var Q39;
            Q39=makeQuery(id+"F14.opExtrude","CAP_EDGE",EDGE,{"disambiguationData":[OSD([sQuery(id+"F13.wireOp",EDGE,"E68.1.1.0")])],"isStart":false});
            var Q40;
            Q40=makeQuery(id+"F14.opExtrude","CAP_EDGE",EDGE,{"disambiguationData":[OSD([sQuery(id+"F13.wireOp",EDGE,"E68.0.1.1")])],"isStart":false});
            var Q41;
            Q41=makeQuery(id+"F14.opExtrude","CAP_EDGE",EDGE,{"disambiguationData":[OSD([sQuery(id+"F13.wireOp",EDGE,"E68.0.1.0")])],"isStart":false});
            var Q42;
            Q42=makeQuery(id+"F14.opExtrude","CAP_EDGE",EDGE,{"disambiguationData":[OSD([sQuery(id+"F13.wireOp",EDGE,"E68.3.1.0")])],"isStart":false});
            var Q43;
            Q43=makeQuery(id+"F14.opExtrude","CAP_EDGE",EDGE,{"disambiguationData":[OSD([sQuery(id+"F13.wireOp",EDGE,"E68.3.1.1")])],"isStart":false});
            fillet(context, id + "F18", {"entities" : qUnion([Q0, Q1, Q2, Q3, Q4, Q5, Q6, Q7, Q8, Q9, Q10, Q11, Q12, Q13, Q14, Q15, Q16, Q17, Q18, Q19, Q20, Q21, Q22, Q23, Q24, Q25, Q26, Q27, Q28, Q29, Q30, Q31, Q32, Q33, Q34, Q35, Q36, Q37, Q38, Q39, Q40, Q41, Q42, Q43]), "radius" : 0.5 * mm, "tangentPropagation" : true, "allowEdgeOverflow" : false});
        }
    });
